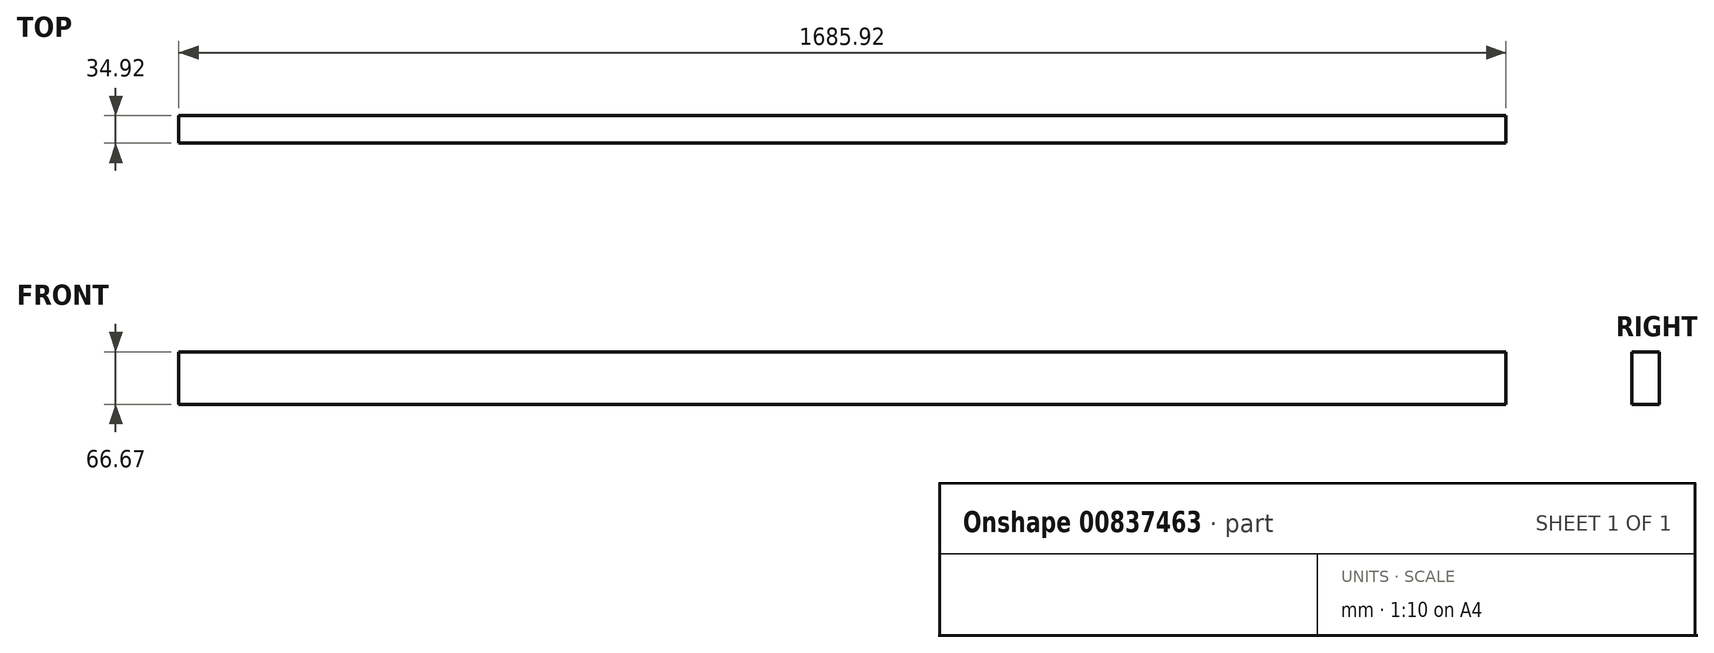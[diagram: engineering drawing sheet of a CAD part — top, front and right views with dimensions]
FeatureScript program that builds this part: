
annotation { "Feature Type Name" : "Feature", "Feature Type Description" : "" }
export const myFeature = defineFeature(function(context is Context, id is Id, definition is map)
    precondition{}
    {
        {
            var Q0;
            Q0=qCreatedBy(makeId("Right.planeOp"),FACE);
            var sketch = newSketch(context, id + "F0", { "sketchPlane" : qUnion([Q0])});
            skLineSegment(sketch, "E0.bottom", {"start": v(0, 0) * mm, "end": v(34.93, 0) * mm});
            skLineSegment(sketch, "E0.top", {"start": v(0, 66.68) * mm, "end": v(34.92, 66.68) * mm});
            skLineSegment(sketch, "E0.left", {"start": v(0, 0) * mm, "end": v(0, 66.68) * mm});
            skLineSegment(sketch, "E0.right", {"start": v(34.93, 0) * mm, "end": v(34.92, 66.68) * mm});
            skSolve(sketch);
        }
        {
            var Q0;
            Q0=makeQuery(id+"F0.imprint","IMPRINT",FACE,{"disambiguationData":[TD([[makeQuery(id+"F0.imprint","IMPRINT",EDGE,{"derivedFrom":sQuery(id+"F0.wireOp",EDGE,"E0.bottom")}),1.0]])]});
            extrude(context, id + "F1", {"entities" : qUnion([Q0]), "endBound" : BoundingType.SYMMETRIC, "depth" : 1685.92 * mm, "offsetDistance" : 25.4 * mm});
        }
    });
